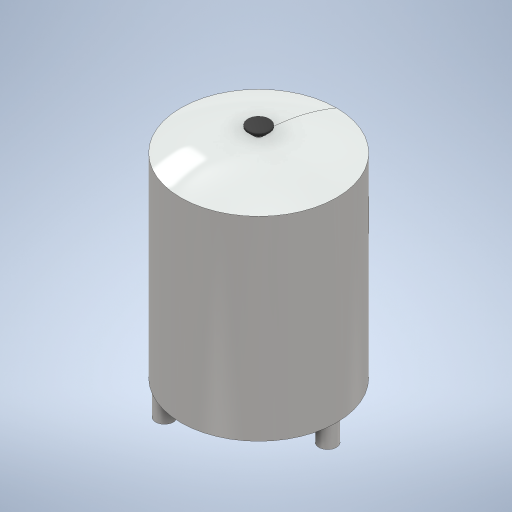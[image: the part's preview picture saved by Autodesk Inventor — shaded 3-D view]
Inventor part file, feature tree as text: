
AUTODESK INVENTOR PART (.ipt)
format: ipt  version: 2024 (Build 280153000, 153)  size: 346,624 bytes
history: native  units: mm
features: sketch x10, extrude x8, plane x4, pattern_circular x1, revolve x1, chamfer x1
ambient origin geometry x8: Origin, YZ Plane, XZ Plane, XY Plane, X Axis, Y Axis, Z Axis, Center Point
bodies: Solid1 (feature_tree)
feature tree (25):
  extrude  "Extrusion1"  Depth=240.0mm
  extrude  "Extrusion2"  Depth=3.0mm TaperAngle=0.0deg
  extrude  "Extrusion3"  Depth=40.0mm TaperAngle=0.0deg
  pattern_circular  "Circular Pattern1"  Count=3 Angle=360.0deg
  revolve  "Revolution1"  Angle=90.0deg
  plane  "Work Plane2"
  sketch  "Sketch5"  dims[d15=15.0mm d16=5.0mm d17=0.0mm]
  extrude  "Extrusion4"  Depth=5.0mm TaperAngle=0.0deg
  extrude  "Extrusion5"  Depth=10.0mm TaperAngle=0.0deg
  chamfer  "Chamfer1"  Distance=7.0mm Angle=45.0deg
  plane  "Work Plane3"
  extrude  "Extrusion6"  Depth=40.0mm
  plane  "Work Plane4"
  extrude  "Extrusion8"  Depth=60.0mm TaperAngle=0.0deg
  plane  "Work Plane5"
  extrude  "Extrusion9"  Depth=60.0mm
  sketch  "Sketch1"  dims[d0=290.0mm d1=240.0mm]
  sketch  "Sketch2"  dims[d2=360.0mm d3=0.0mm d4=3.0mm d5=0.0mm]
  sketch  "Sketch3"  dims[d6=33.0mm d7=40.0mm d8=0.0mm d9=30.0mm d10=360.0deg]
  sketch  "Sketch4"  dims[d13=30.0mm d14=90.0deg]
  sketch  "Sketch6"  dims[d18=40.0mm d19=10.0mm d20=0.0mm d21=7.0mm d22=2.0mm d23=45.0deg]
  sketch  "Sketch7"  dims[d24=40.0mm d25=20.0mm]
  sketch  "Sketch8"  dims[d26=30.0mm d27=0.0mm d31=60.0mm d32=0.0mm]
  sketch  "Sketch11"  dims[d33=80.0mm d34=60.0mm]
  sketch  "Sketch12"  dims[d35=200.0mm d36=40.0mm d37=0.0mm]
